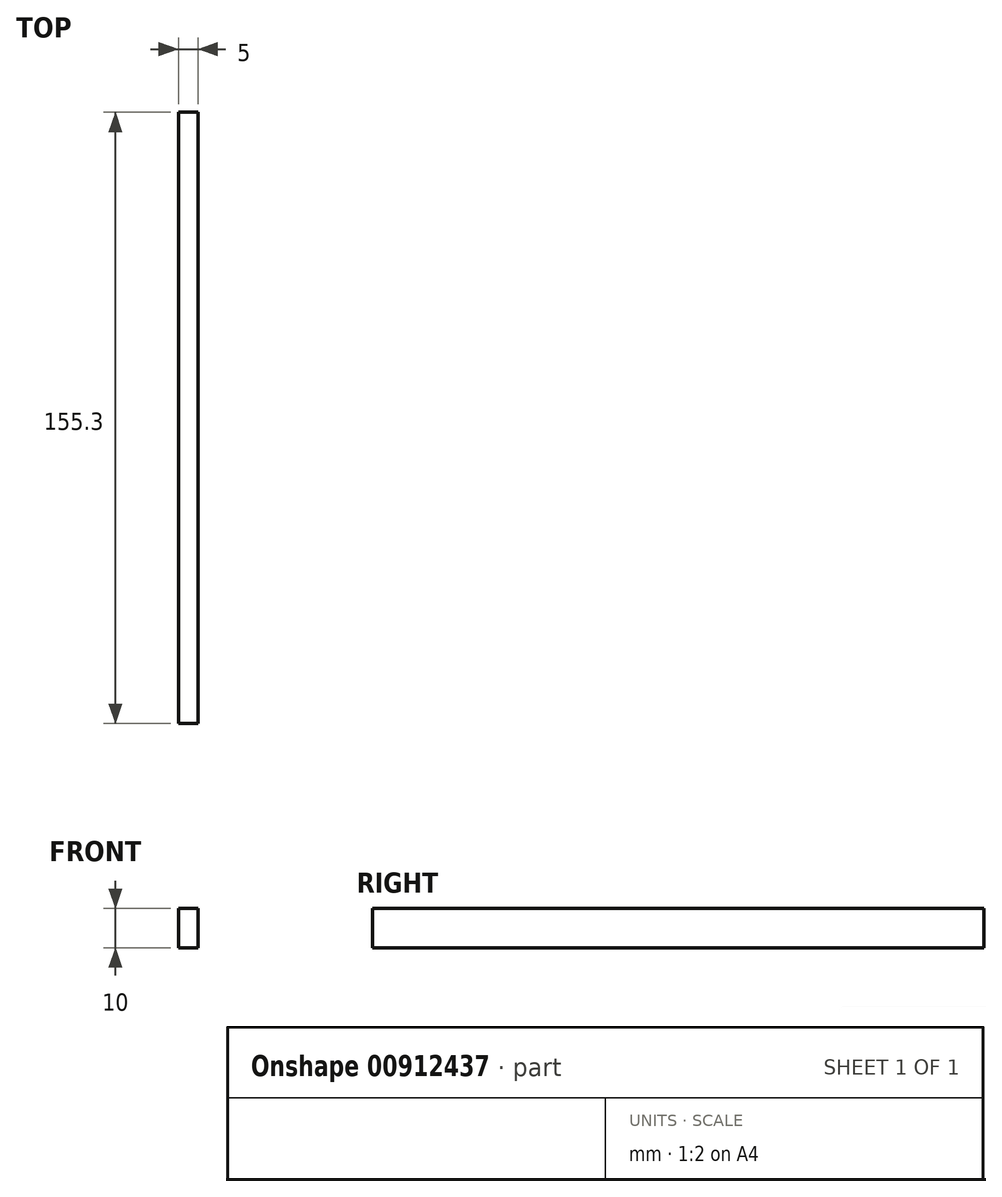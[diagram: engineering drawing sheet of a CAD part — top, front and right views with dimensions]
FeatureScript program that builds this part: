
annotation { "Feature Type Name" : "Feature", "Feature Type Description" : "" }
export const myFeature = defineFeature(function(context is Context, id is Id, definition is map)
    precondition{}
    {
        {
            var Q0;
            Q0=qCreatedBy(makeId("Front.planeOp"),FACE);
            var sketch = newSketch(context, id + "F0", { "sketchPlane" : qUnion([Q0])});
            skLineSegment(sketch, "E0.bottom", {"start": v(2.5, 5) * mm, "end": v(-2.5, 5) * mm});
            skLineSegment(sketch, "E0.top", {"start": v(2.5, -5) * mm, "end": v(-2.5, -5) * mm});
            skLineSegment(sketch, "E0.left", {"start": v(2.5, 5) * mm, "end": v(2.5, -5) * mm});
            skLineSegment(sketch, "E0.right", {"start": v(-2.5, 5) * mm, "end": v(-2.5, -5) * mm});
            skPoint(sketch, "E0.middle", {"position": v(0, 0) * mm});
            skSolve(sketch);
        }
        {
            var Q0;
            Q0 = qSketchRegion(id + "F0", true);
            extrude(context, id + "F1", {"entities" : qUnion([Q0]), "depth" : 155.3 * mm, "offsetDistance" : 25 * mm});
        }
    });
